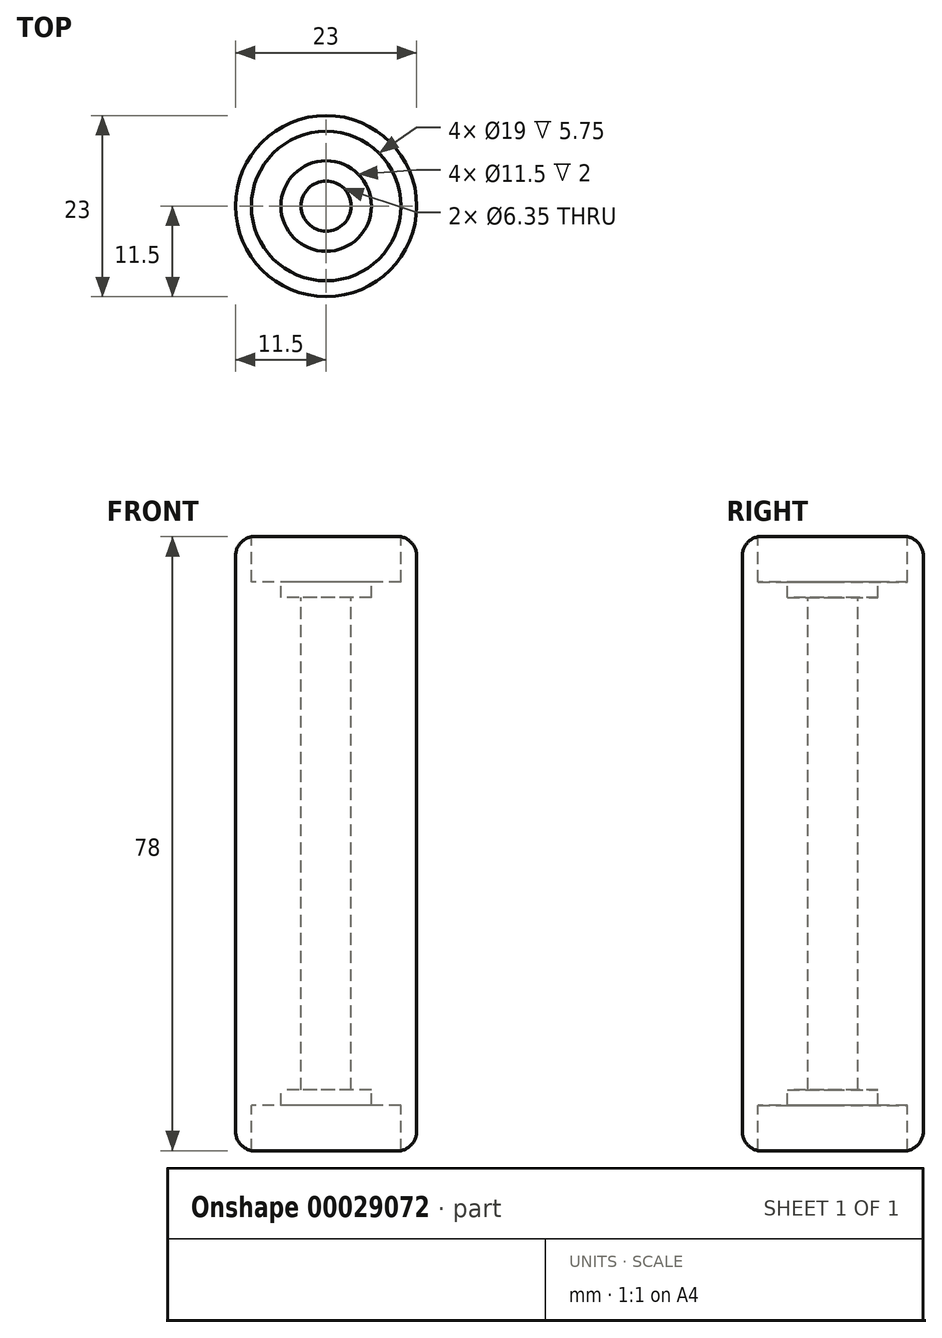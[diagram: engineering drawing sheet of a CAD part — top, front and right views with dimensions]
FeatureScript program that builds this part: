
annotation { "Feature Type Name" : "Feature", "Feature Type Description" : "" }
export const myFeature = defineFeature(function(context is Context, id is Id, definition is map)
    precondition{}
    {
        {
            var Q0;
            Q0=qCreatedBy(makeId("Front.planeOp"),FACE);
            var sketch = newSketch(context, id + "F0", { "sketchPlane" : qUnion([Q0])});
            skLineSegment(sketch, "E0", {"start": v(9.5, 33.25) * mm, "end": v(9.5, 39) * mm});
            skLineSegment(sketch, "E1", {"start": v(9.5, 39) * mm, "end": v(11.5, 39) * mm});
            skLineSegment(sketch, "E2", {"start": v(11.5, 39) * mm, "end": v(11.5, -39) * mm});
            skLineSegment(sketch, "E3", {"start": v(11.5, -39) * mm, "end": v(9.5, -39) * mm});
            skLineSegment(sketch, "E4", {"start": v(9.5, -39) * mm, "end": v(9.5, -33.25) * mm});
            skLineSegment(sketch, "E5", {"start": v(9.5, 33.25) * mm, "end": v(5.75, 33.25) * mm});
            skLineSegment(sketch, "E6", {"start": v(3.17, 31.25) * mm, "end": v(3.18, -31.25) * mm});
            skLineSegment(sketch, "E7", {"start": v(5.75, -33.25) * mm, "end": v(9.5, -33.25) * mm});
            skPoint(sketch, "E8", {"position": v(3.18, 0) * mm});
            skLineSegment(sketch, "E9", {"start": v(0, 39) * mm, "end": v(0, -39) * mm, "construction": true});
            skLineSegment(sketch, "E10", {"start": v(5.75, 33.25) * mm, "end": v(5.75, 31.25) * mm});
            skLineSegment(sketch, "E11", {"start": v(5.75, 31.25) * mm, "end": v(3.17, 31.25) * mm});
            skPoint(sketch, "E12.orphan", {"position": v(3.18, 33.25) * mm});
            skLineSegment(sketch, "E13", {"start": v(5.75, -33.25) * mm, "end": v(5.75, -31.25) * mm});
            skLineSegment(sketch, "E14", {"start": v(5.75, -31.25) * mm, "end": v(3.18, -31.25) * mm});
            skPoint(sketch, "E15.orphan", {"position": v(3.18, -33.25) * mm});
            skSolve(sketch);
        }
        {
            var Q0;
            Q0 = qSketchRegion(id + "F0", true);
            var Q1;
            Q1=sQuery(id+"F0.wireOp",EDGE,"E9");
            revolve(context, id + "F1", {"entities" : qUnion([Q0]), "axis" : qUnion([Q1]), "revolveType" : RevolveType.FULL});
        }
        {
            var Q0;
            Q0=makeQuery(id+"F1.opRevolve","SWEPT_EDGE",EDGE,{"disambiguationData":[OSD([sQuery(id+"F0.wireOp",EDGE,"E1"),sQuery(id+"F0.wireOp",EDGE,"E2")])]});
            var Q1;
            Q1=makeQuery(id+"F1.opRevolve","SWEPT_EDGE",EDGE,{"disambiguationData":[OSD([sQuery(id+"F0.wireOp",EDGE,"E2"),sQuery(id+"F0.wireOp",EDGE,"E3")])]});
            fillet(context, id + "F2", {"entities" : qUnion([Q0, Q1]), "radius" : 2.54 * mm, "tangentPropagation" : true, "allowEdgeOverflow" : false});
        }
    });
